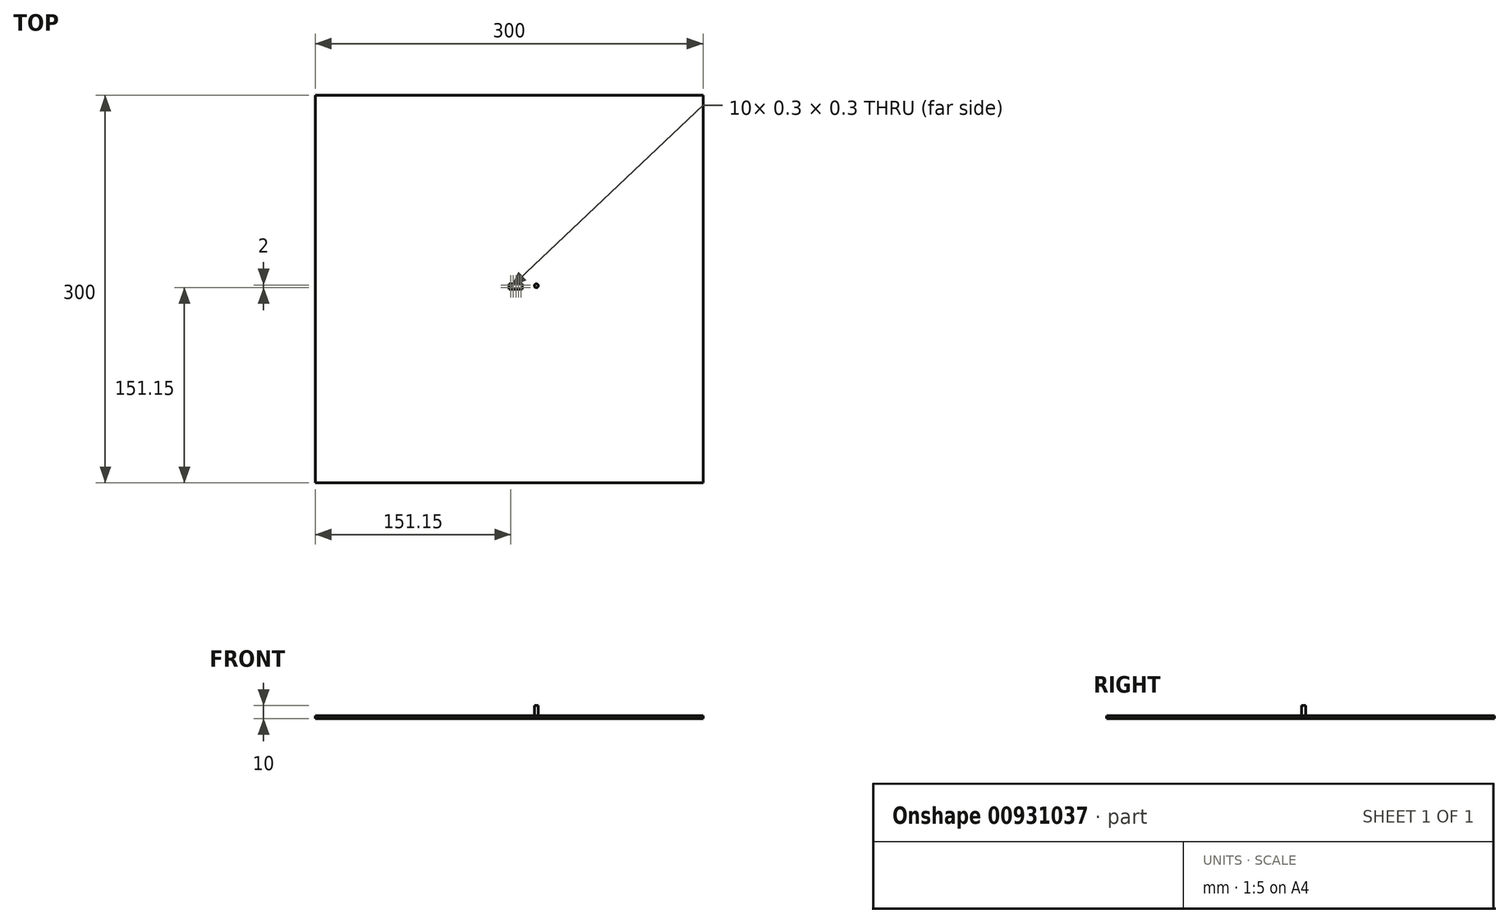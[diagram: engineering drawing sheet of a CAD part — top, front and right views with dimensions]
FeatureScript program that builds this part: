
annotation { "Feature Type Name" : "Feature", "Feature Type Description" : "" }
export const myFeature = defineFeature(function(context is Context, id is Id, definition is map)
    precondition{}
    {
        {
            var Q0;
            Q0=qCreatedBy(makeId("Top.planeOp"),FACE);
            var sketch = newSketch(context, id + "F0", { "sketchPlane" : qUnion([Q0])});
            skLineSegment(sketch, "E0.bottom", {"start": v(-150, 150) * mm, "end": v(150, 150) * mm});
            skLineSegment(sketch, "E0.top", {"start": v(-150, -150) * mm, "end": v(150, -150) * mm});
            skLineSegment(sketch, "E0.left", {"start": v(-150, 150) * mm, "end": v(-150, -150) * mm});
            skLineSegment(sketch, "E0.right", {"start": v(150, 150) * mm, "end": v(150, -150) * mm});
            skLineSegment(sketch, "E1", {"start": v(-150, 150) * mm, "end": v(150, -150) * mm, "construction": true});
            skLineSegment(sketch, "E2", {"start": v(150, 150) * mm, "end": v(-150, -150) * mm, "construction": true});
            skPoint(sketch, "E3", {"position": v(0, 0) * mm});
            skSolve(sketch);
        }
        {
            var Q0;
            Q0 = qSketchRegion(id + "F0", true);
            extrude(context, id + "F1", {"entities" : qUnion([Q0]), "depth" : 2 * mm, "offsetDistance" : 25 * mm});
        }
        {
            var Q0;
            Q0=makeQuery(id+"F1.opExtrude","CAP_FACE",FACE,{"disambiguationData":[OSD([sQuery(id+"F0.wireOp",EDGE,"E0.bottom"),sQuery(id+"F0.wireOp",EDGE,"E0.top"),sQuery(id+"F0.wireOp",EDGE,"E0.left"),sQuery(id+"F0.wireOp",EDGE,"E0.right")])],"isStart":false});
            var sketch = newSketch(context, id + "F2", { "sketchPlane" : qUnion([Q0])});
            skLineSegment(sketch, "E4.bottom", {"start": v(0, 4) * mm, "end": v(10, 4) * mm});
            skLineSegment(sketch, "E4.top", {"start": v(0, 0) * mm, "end": v(10, 0) * mm});
            skLineSegment(sketch, "E4.left", {"start": v(0, 4) * mm, "end": v(0, 0) * mm});
            skLineSegment(sketch, "E4.right", {"start": v(10, 4) * mm, "end": v(10, 0) * mm});
            skSolve(sketch);
        }
        {
            var Q0;
            Q0 = qSketchRegion(id + "F2", true);
            extrude(context, id + "F3", {"entities" : qUnion([Q0]), "operationType" : NewBodyOperationType.REMOVE, "oppositeDirection" : true, "depth" : .1 * mm, "offsetDistance" : 25 * mm});
        }
        {
            var Q0;
            Q0=makeQuery(id+"F1.opExtrude","CAP_FACE",FACE,{"disambiguationData":[OSD([sQuery(id+"F0.wireOp",EDGE,"E0.bottom"),sQuery(id+"F0.wireOp",EDGE,"E0.top"),sQuery(id+"F0.wireOp",EDGE,"E0.left"),sQuery(id+"F0.wireOp",EDGE,"E0.right")])],"isStart":false});
            var sketch = newSketch(context, id + "F4", { "sketchPlane" : qUnion([Q0])});
            skLineSegment(sketch, "E5.bottom", {"start": v(1, 3) * mm, "end": v(1.3, 3) * mm});
            skLineSegment(sketch, "E5.top", {"start": v(1, 3.3) * mm, "end": v(1.3, 3.3) * mm});
            skLineSegment(sketch, "E5.left", {"start": v(1, 3) * mm, "end": v(1, 3.3) * mm});
            skLineSegment(sketch, "E5.right", {"start": v(1.3, 3) * mm, "end": v(1.3, 3.3) * mm});
            skLineSegment(sketch, "E6.0.1.0", {"start": v(1, 1.3) * mm, "end": v(1.3, 1.3) * mm});
            skLineSegment(sketch, "E6.0.1.1", {"start": v(1.3, 1) * mm, "end": v(1.3, 1.3) * mm});
            skLineSegment(sketch, "E6.0.1.2", {"start": v(1, 1) * mm, "end": v(1.3, 1) * mm});
            skLineSegment(sketch, "E6.0.1.3", {"start": v(1, 1) * mm, "end": v(1, 1.3) * mm});
            skLineSegment(sketch, "E6.1.0.0", {"start": v(3, 3.3) * mm, "end": v(3.3, 3.3) * mm});
            skLineSegment(sketch, "E6.1.0.1", {"start": v(3.3, 3) * mm, "end": v(3.3, 3.3) * mm});
            skLineSegment(sketch, "E6.1.0.2", {"start": v(3, 3) * mm, "end": v(3.3, 3) * mm});
            skLineSegment(sketch, "E6.1.0.3", {"start": v(3, 3) * mm, "end": v(3, 3.3) * mm});
            skLineSegment(sketch, "E6.1.1.0", {"start": v(3, 1.3) * mm, "end": v(3.3, 1.3) * mm});
            skLineSegment(sketch, "E6.1.1.1", {"start": v(3.3, 1) * mm, "end": v(3.3, 1.3) * mm});
            skLineSegment(sketch, "E6.1.1.2", {"start": v(3, 1) * mm, "end": v(3.3, 1) * mm});
            skLineSegment(sketch, "E6.1.1.3", {"start": v(3, 1) * mm, "end": v(3, 1.3) * mm});
            skLineSegment(sketch, "E6.2.0.0", {"start": v(5, 3.3) * mm, "end": v(5.3, 3.3) * mm});
            skLineSegment(sketch, "E6.2.0.1", {"start": v(5.3, 3) * mm, "end": v(5.3, 3.3) * mm});
            skLineSegment(sketch, "E6.2.0.2", {"start": v(5, 3) * mm, "end": v(5.3, 3) * mm});
            skLineSegment(sketch, "E6.2.0.3", {"start": v(5, 3) * mm, "end": v(5, 3.3) * mm});
            skLineSegment(sketch, "E6.2.1.0", {"start": v(5, 1.3) * mm, "end": v(5.3, 1.3) * mm});
            skLineSegment(sketch, "E6.2.1.1", {"start": v(5.3, 1) * mm, "end": v(5.3, 1.3) * mm});
            skLineSegment(sketch, "E6.2.1.2", {"start": v(5, 1) * mm, "end": v(5.3, 1) * mm});
            skLineSegment(sketch, "E6.2.1.3", {"start": v(5, 1) * mm, "end": v(5, 1.3) * mm});
            skLineSegment(sketch, "E6.3.0.0", {"start": v(7, 3.3) * mm, "end": v(7.3, 3.3) * mm});
            skLineSegment(sketch, "E6.3.0.1", {"start": v(7.3, 3) * mm, "end": v(7.3, 3.3) * mm});
            skLineSegment(sketch, "E6.3.0.2", {"start": v(7, 3) * mm, "end": v(7.3, 3) * mm});
            skLineSegment(sketch, "E6.3.0.3", {"start": v(7, 3) * mm, "end": v(7, 3.3) * mm});
            skLineSegment(sketch, "E6.3.1.0", {"start": v(7, 1.3) * mm, "end": v(7.3, 1.3) * mm});
            skLineSegment(sketch, "E6.3.1.1", {"start": v(7.3, 1) * mm, "end": v(7.3, 1.3) * mm});
            skLineSegment(sketch, "E6.3.1.2", {"start": v(7, 1) * mm, "end": v(7.3, 1) * mm});
            skLineSegment(sketch, "E6.3.1.3", {"start": v(7, 1) * mm, "end": v(7, 1.3) * mm});
            skLineSegment(sketch, "E6.4.0.0", {"start": v(9, 3.3) * mm, "end": v(9.3, 3.3) * mm});
            skLineSegment(sketch, "E6.4.0.1", {"start": v(9.3, 3) * mm, "end": v(9.3, 3.3) * mm});
            skLineSegment(sketch, "E6.4.0.2", {"start": v(9, 3) * mm, "end": v(9.3, 3) * mm});
            skLineSegment(sketch, "E6.4.0.3", {"start": v(9, 3) * mm, "end": v(9, 3.3) * mm});
            skLineSegment(sketch, "E6.4.1.0", {"start": v(9, 1.3) * mm, "end": v(9.3, 1.3) * mm});
            skLineSegment(sketch, "E6.4.1.1", {"start": v(9.3, 1) * mm, "end": v(9.3, 1.3) * mm});
            skLineSegment(sketch, "E6.4.1.2", {"start": v(9, 1) * mm, "end": v(9.3, 1) * mm});
            skLineSegment(sketch, "E6.4.1.3", {"start": v(9, 1) * mm, "end": v(9, 1.3) * mm});
            skLineSegment(sketch, "E6.direction1", {"start": v(1, 3.3) * mm, "end": v(3, 3.3) * mm, "construction": true});
            skLineSegment(sketch, "E6.direction2", {"start": v(1, 3.3) * mm, "end": v(1, 1.3) * mm, "construction": true});
            skLineSegment(sketch, "E7", {"start": v(19.5, 4) * mm, "end": v(-3.13, 4) * mm, "construction": true});
            skSolve(sketch);
        }
        {
            var Q0;
            Q0 = qSketchRegion(id + "F4", true);
            extrude(context, id + "F5", {"entities" : qUnion([Q0]), "operationType" : NewBodyOperationType.REMOVE, "oppositeDirection" : true, "depth" : 3 * mm, "offsetDistance" : 25 * mm});
        }
        {
            var Q0;
            Q0=qCreatedBy(makeId("Top.planeOp"),FACE);
            var sketch = newSketch(context, id + "F6", { "sketchPlane" : qUnion([Q0])});
            skCircle(sketch, "E8", {"center": v(21, 2.5) * mm, "radius": 1.5 * mm});
            skLineSegment(sketch, "E9", {"start": v(0.6, 4) * mm, "end": v(25.6, 4) * mm, "construction": true});
            skSolve(sketch);
        }
        {
            var Q0;
            Q0 = qSketchRegion(id + "F6", true);
            extrude(context, id + "F7", {"entities" : qUnion([Q0]), "operationType" : NewBodyOperationType.ADD, "depth" : 10 * mm, "offsetDistance" : 25 * mm});
        }
    });
